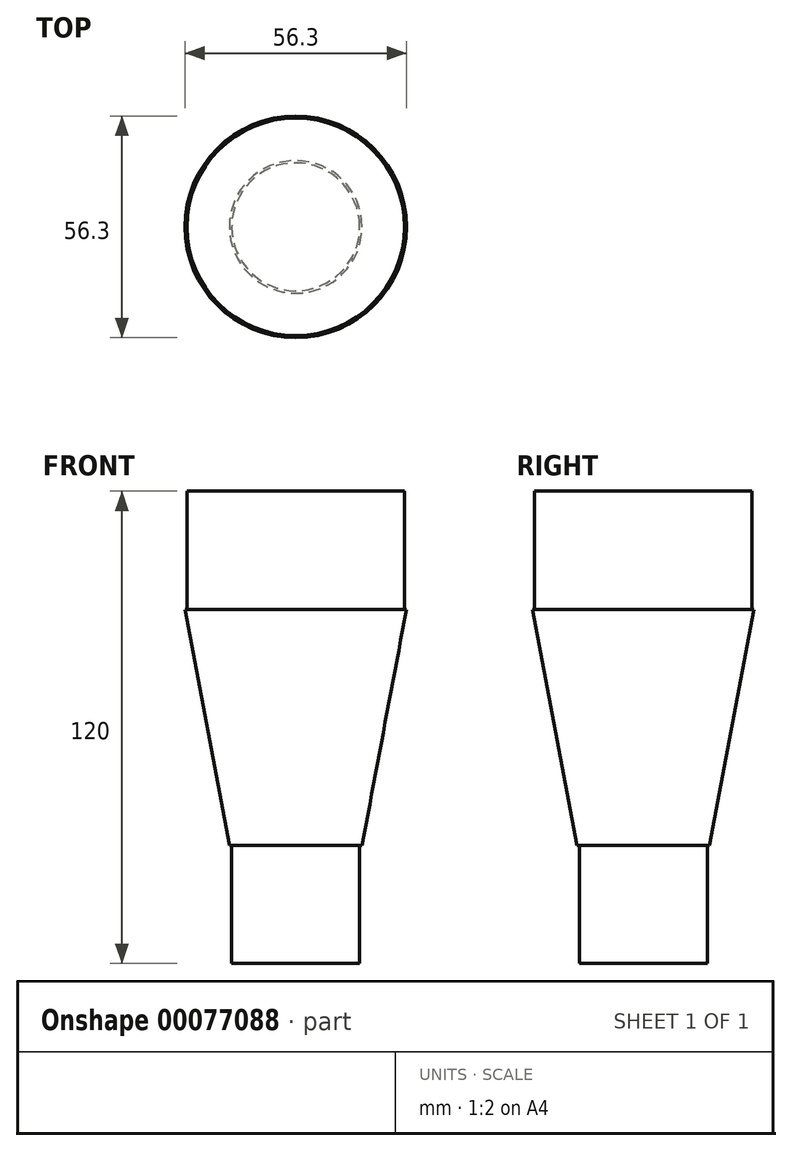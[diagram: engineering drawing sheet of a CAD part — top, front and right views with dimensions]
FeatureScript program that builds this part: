
annotation { "Feature Type Name" : "Feature", "Feature Type Description" : "" }
export const myFeature = defineFeature(function(context is Context, id is Id, definition is map)
    precondition{}
    {
        {
            var Q0;
            Q0=qCreatedBy(makeId("Front.planeOp"),FACE);
            var sketch = newSketch(context, id + "F0", { "sketchPlane" : qUnion([Q0])});
            skLineSegment(sketch, "E0", {"start": v(-27.65, 73.27) * mm, "end": v(-27.65, 43.27) * mm});
            skLineSegment(sketch, "E1", {"start": v(-27.65, 43.27) * mm, "end": v(-28.15, 43.27) * mm});
            skLineSegment(sketch, "E2", {"start": v(-28.15, 43.27) * mm, "end": v(-16.85, -16.73) * mm});
            skLineSegment(sketch, "E3", {"start": v(-16.85, -16.73) * mm, "end": v(-16.25, -16.73) * mm});
            skLineSegment(sketch, "E4", {"start": v(-16.25, -16.73) * mm, "end": v(-16.25, -46.73) * mm});
            skLineSegment(sketch, "E5", {"start": v(-16.25, -46.73) * mm, "end": v(0, -46.73) * mm});
            skLineSegment(sketch, "E6", {"start": v(-27.65, 73.27) * mm, "end": v(0, 73.27) * mm});
            skLineSegment(sketch, "E7", {"start": v(0, 94.78) * mm, "end": v(0, -99.97) * mm, "construction": true});
            skLineSegment(sketch, "E8", {"start": v(0, 73.27) * mm, "end": v(0, -46.73) * mm});
            skSolve(sketch);
        }
        {
            var Q0;
            Q0=makeQuery(id+"F0.imprint","IMPRINT",FACE,{"disambiguationData":[TD([[makeQuery(id+"F0.imprint","IMPRINT",EDGE,{"derivedFrom":sQuery(id+"F0.wireOp",EDGE,"E0")}),1.0]])]});
            var Q1;
            Q1=sQuery(id+"F0.wireOp",EDGE,"E7");
            revolve(context, id + "F1", {"entities" : qUnion([Q0]), "axis" : qUnion([Q1]), "revolveType" : RevolveType.FULL});
        }
    });
